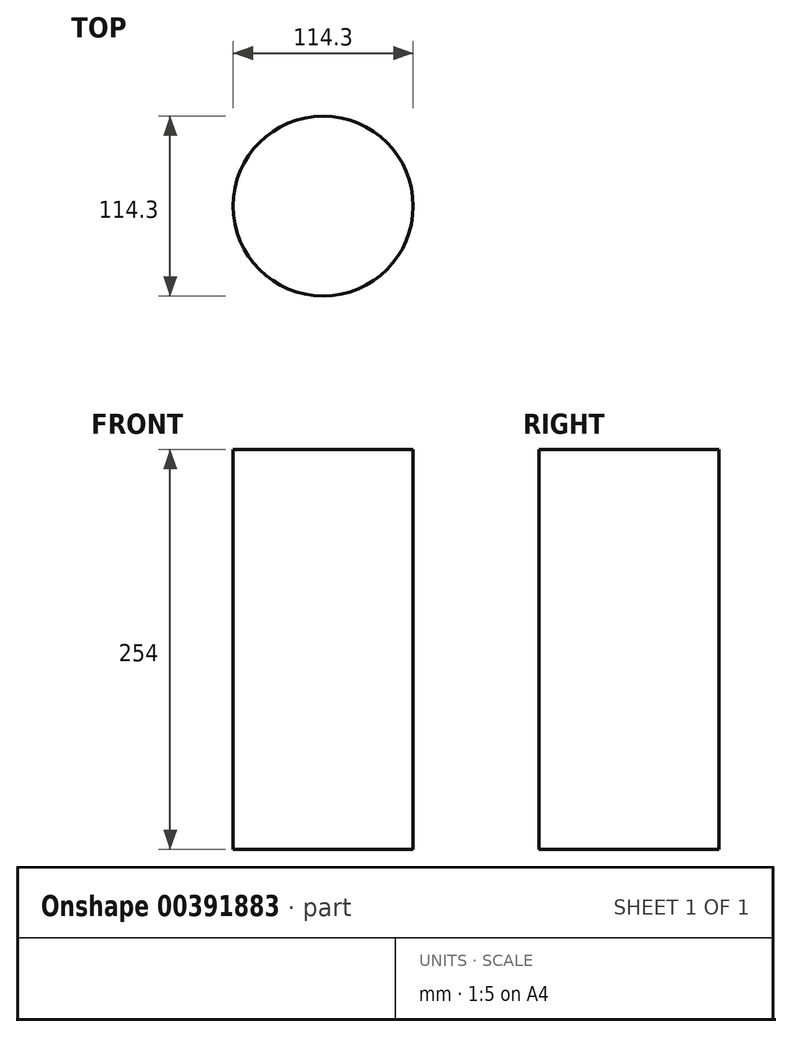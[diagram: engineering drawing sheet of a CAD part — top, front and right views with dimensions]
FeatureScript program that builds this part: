
annotation { "Feature Type Name" : "Feature", "Feature Type Description" : "" }
export const myFeature = defineFeature(function(context is Context, id is Id, definition is map)
    precondition{}
    {
        {
            var Q0;
            Q0=qCreatedBy(makeId("Top.planeOp"),FACE);
            var sketch = newSketch(context, id + "F0", { "sketchPlane" : qUnion([Q0])});
            skCircle(sketch, "E0", {"center": v(0, -3.32) * mm, "radius": 57.15 * mm});
            skSolve(sketch);
        }
        {
            var Q0;
            Q0 = qSketchRegion(id + "F0", true);
            extrude(context, id + "F1", {"entities" : qUnion([Q0]), "endBound" : BoundingType.SYMMETRIC, "depth" : 254 * mm});
        }
    });
